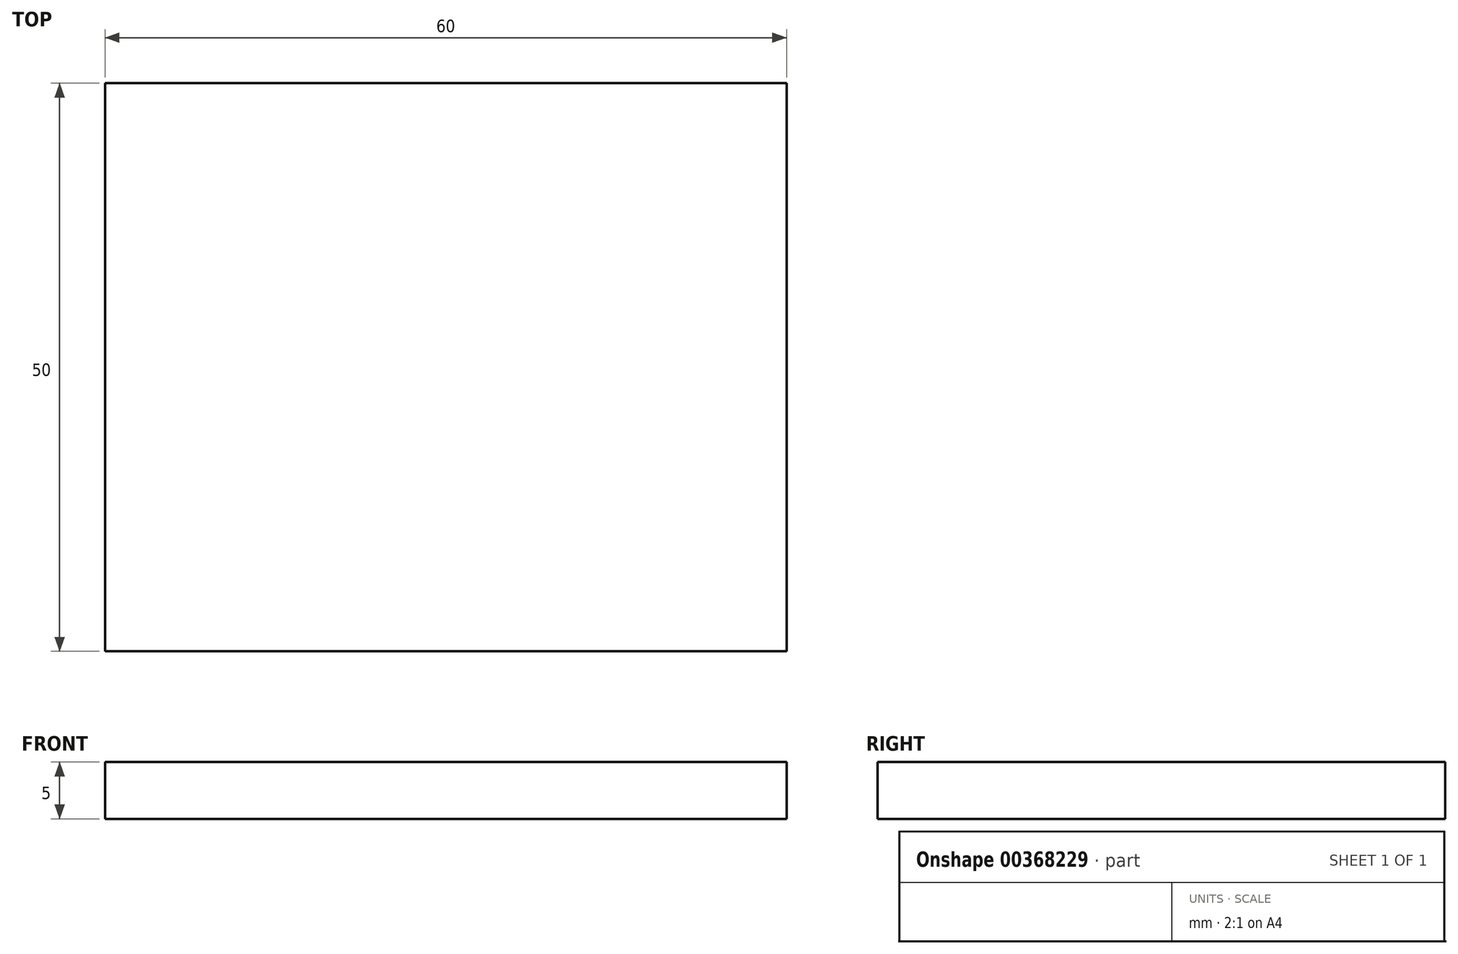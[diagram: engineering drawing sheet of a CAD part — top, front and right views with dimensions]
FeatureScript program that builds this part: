
annotation { "Feature Type Name" : "Feature", "Feature Type Description" : "" }
export const myFeature = defineFeature(function(context is Context, id is Id, definition is map)
    precondition{}
    {
        {
            var Q0;
            Q0=qCreatedBy(makeId("Top.planeOp"),FACE);
            var sketch = newSketch(context, id + "F0", { "sketchPlane" : qUnion([Q0])});
            skLineSegment(sketch, "E0.bottom", {"start": v(-30, -25) * mm, "end": v(30, -25) * mm});
            skLineSegment(sketch, "E0.top", {"start": v(-30, 25) * mm, "end": v(30, 25) * mm});
            skLineSegment(sketch, "E0.left", {"start": v(-30, -25) * mm, "end": v(-30, 25) * mm});
            skLineSegment(sketch, "E0.right", {"start": v(30, -25) * mm, "end": v(30, 25) * mm});
            skLineSegment(sketch, "E1", {"start": v(-30, 0) * mm, "end": v(30, 0) * mm, "construction": true});
            skLineSegment(sketch, "E2", {"start": v(0, 25) * mm, "end": v(0, -25) * mm, "construction": true});
            skPoint(sketch, "E3", {"position": v(5, 0) * mm});
            skSolve(sketch);
        }
        {
            var Q0;
            Q0=makeQuery(id+"F0.imprint","IMPRINT",FACE,{"disambiguationData":[TD([[makeQuery(id+"F0.imprint","IMPRINT",EDGE,{"derivedFrom":sQuery(id+"F0.wireOp",EDGE,"E0.bottom")}),1.0]])]});
            extrude(context, id + "F1", {"entities" : qUnion([Q0]), "oppositeDirection" : true, "depth" : 5 * mm});
        }
    });
